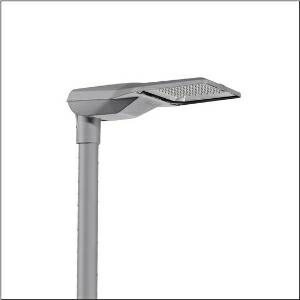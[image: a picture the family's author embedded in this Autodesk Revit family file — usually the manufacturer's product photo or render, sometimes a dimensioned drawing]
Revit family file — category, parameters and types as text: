
# Revit family: streetlight_sl_21_iq_midi___p0_8a_5xe3u31g08nb_121e
name_source: partatom
category: Lighting Fixtures
units: mm (PartAtom-declared; Revit-internal decimal feet)

## family parameters
Cut with Voids When Loaded = No
Host = Face
Light Source = No
Part Type = Normal
Room Calculation Point = No
Round Connector Dimension = Use Diameter
Shared = No

## types (1)
- --- (1 x LED, 23430 lm, 155.5 W, 3000K)
    Apparent Load = 155 VA
    CIE Flux Codes = 36 69 97 100 100
    Color Rendering = 70
    Color Temperature = 3000K
    Default Elevation = 1800 mm
    Description = Streetlight SL 21 iQ midi, mast luminaire, primary light control with lens, of PMMA, primary optical cover: cover, of toughened safety glass, transparent, light distribution: P0.8a, light emission: direct distribution, primary light characteristic: asymmetric, installation type: post-top, side-entry, LED, High Power LED, rated luminous flux: 23.430lm, luminous efficacy: 151lm/W, light colour: 730, colour temperature: 3000K, control gear: iQ Street-Remote, control: pre-setting: linear dimming characteristic, Street-Remote, Auto-Match, Temp-Guard, Lumen-Switch, Night-Set, Smart-Wire, Light-Fading, Desk-Remote (wireless, voltage-free reading and setting of iQ features in the workshop via application-optimized NFC function/RFID function), optimised constant luminous flux control (CLO 2.0), mains connection: 230..240V, AC, 50/60Hz, start of lifetime: 156W, end of service life: 162W, reduction: 69W, luminaire housing, of diecast aluminium, powder-coated, SITECO metallic grey (DB 702S), corrosivity category C5 high according to DIN EN ISO 12944, please order mast flange separately, inclination adjustable: 0°, 5°, 10°, 15°, sealing non-destructively replaceable, multi-level sealing system, length: 644mm, width: 335mm, height: 110mm, mast flange for spigot size: 42mm (side-entry): 5XC10008XM4, 60/48mm (side-entry/post-top): 5XC10108XM2, 76/60mm (side-entry/post-top): 5XC10108XM1, mounting height: 4..8m, protection rating (complete): IP66, insulation class (complete): insulation class II (safety insulation), certification: CE, ENEC, ENEC+, VDE, impact resistance: IK10, permissible operating ambient temperature for outdoor applications: -40..+50°C, standard-compliant lighting for roads and squares, packaging unit: 1 piece

Light Distribution: P0.8a
    Height = 111 mm
    Lamp = 1 x LED
    Lamp Light Flux = 23430 lm
    Lamp Power = 155.5 W
    Lamp count = 1
    Length = 644 mm
    Luminous efficacy = 151 lm/W
    Manufacturer = Siteco
    ModVariant = No
    Model = 5XE3U31G08NB
    Number of Poles = 1
    OnlyDefault = Yes
    Power Factor = 1
    Product Name = Streetlight SL 21 iQ midi | P0.8a
    Product group = mast luminaire | pylon top
    ProductGroupID = 6100
    Protection Class = Protection class II
    Protection Degree = IP 66
    RLX_Detail_Level = 1
    RLX_Emergency_Light_Flux = 0 lm
    RLX_Emergency_Type = 0
    RLX_Emergency_Type_DB = No
    RlxData = <blob elided: 90633 chars, md5=e1afc92b>
    Socket = socket
    Standby Power = 0 W
    System Light Flux = 23431 lm
    System Power = 155 W
    Type Comments = factory setting: luminous flux: 100 % | dim-lin: 254 | 823 mA
    Type Image = l_1004298.jpg
    URL = http://relux.com
    VarID = @adj_079257
    Voltage = 0 V
    Weight = 0.00 kg
    Width = 336 mm

## geometry (parser evidence)
native form markers: Blend x4, Sweep x11
no freeform markers — native parametric forms only
